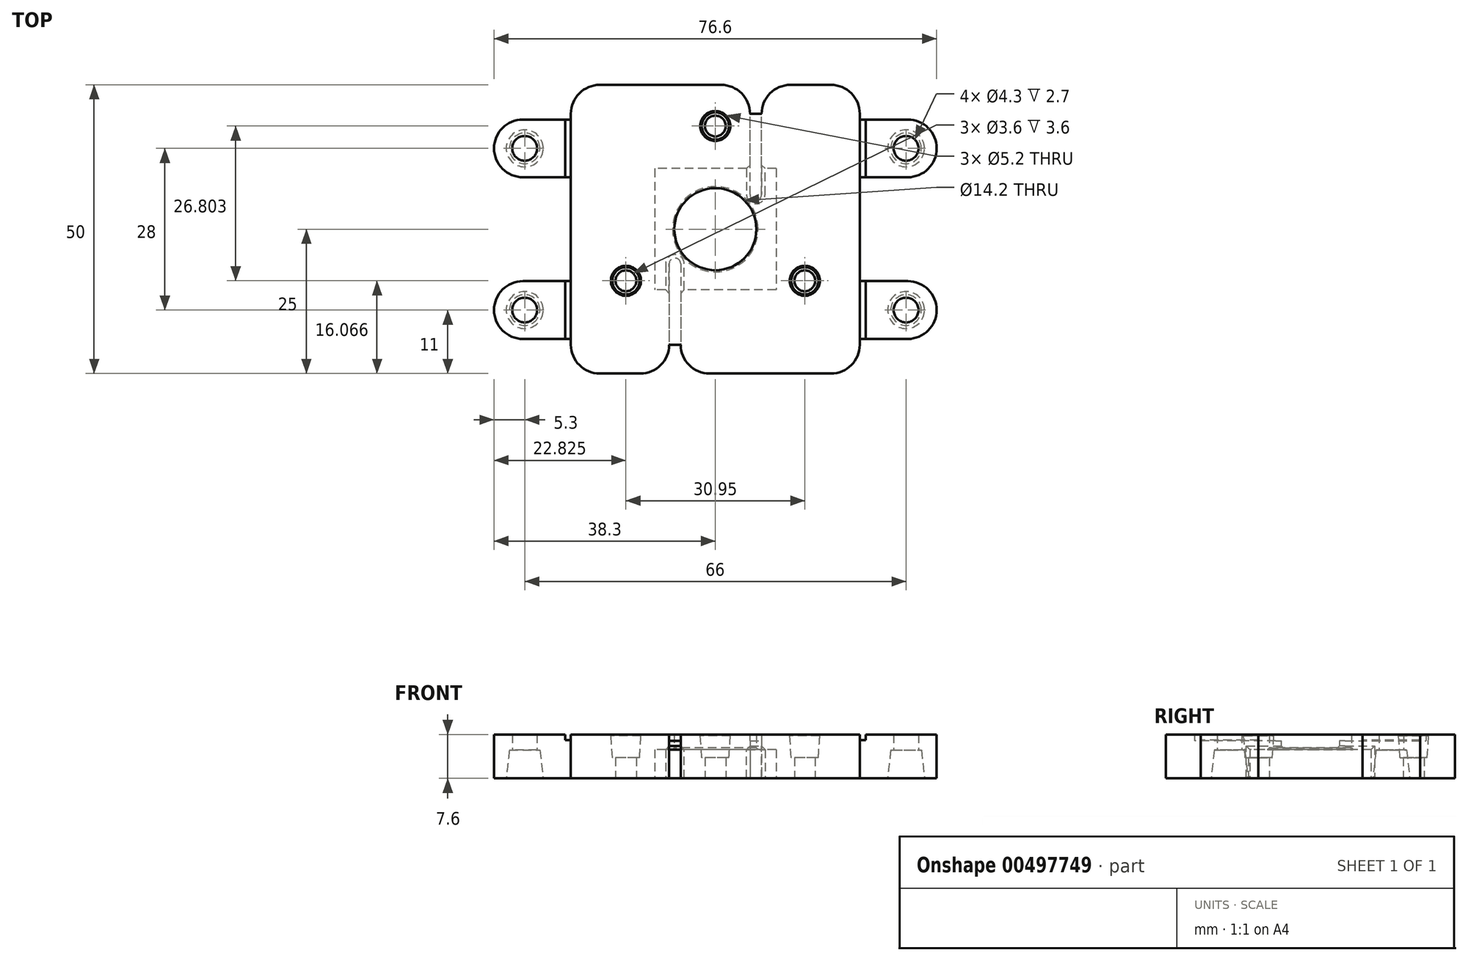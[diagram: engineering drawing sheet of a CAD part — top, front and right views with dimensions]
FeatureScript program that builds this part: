
annotation { "Feature Type Name" : "Feature", "Feature Type Description" : "" }
export const myFeature = defineFeature(function(context is Context, id is Id, definition is map)
    precondition{}
    {
        {
            var Q0;
            Q0=qCreatedBy(makeId("Top.planeOp"),FACE);
            var sketch = newSketch(context, id + "F0", { "sketchPlane" : qUnion([Q0])});
            skLineSegment(sketch, "E0.bottom", {"start": v(10.5, 10.5) * mm, "end": v(-10.5, 10.5) * mm});
            skLineSegment(sketch, "E0.top", {"start": v(10.5, -10.5) * mm, "end": v(-10.5, -10.5) * mm});
            skLineSegment(sketch, "E0.left", {"start": v(10.5, 10.5) * mm, "end": v(10.5, -10.5) * mm});
            skLineSegment(sketch, "E0.right", {"start": v(-10.5, 10.5) * mm, "end": v(-10.5, -10.5) * mm});
            skPoint(sketch, "E0.middle", {"position": v(0, 0) * mm});
            skLineSegment(sketch, "E1.bottom", {"start": v(25, 25) * mm, "end": v(-25, 25) * mm});
            skLineSegment(sketch, "E1.top", {"start": v(25, -25) * mm, "end": v(-25, -25) * mm});
            skLineSegment(sketch, "E1.left", {"start": v(25, 25) * mm, "end": v(25, -25) * mm});
            skLineSegment(sketch, "E1.right", {"start": v(-25, 25) * mm, "end": v(-25, -25) * mm});
            skCircle(sketch, "E2", {"center": v(-15.48, -8.93) * mm, "radius": 1.8 * mm});
            skCircle(sketch, "E3", {"center": v(0, 17.87) * mm, "radius": 1.8 * mm});
            skCircle(sketch, "E4", {"center": v(15.47, -8.93) * mm, "radius": 1.8 * mm});
            skLineSegment(sketch, "E5", {"start": v(-15.48, -8.93) * mm, "end": v(0, 17.87) * mm, "construction": true});
            skLineSegment(sketch, "E6", {"start": v(15.48, -8.93) * mm, "end": v(0, 17.87) * mm, "construction": true});
            skLineSegment(sketch, "E7", {"start": v(15.47, -8.93) * mm, "end": v(-15.48, -8.93) * mm, "construction": true});
            skCircle(sketch, "E8", {"center": v(0, 0) * mm, "radius": 17.87 * mm, "construction": true});
            skLineSegment(sketch, "E9.bottom", {"start": v(-25, 19) * mm, "end": v(-38.3, 19) * mm});
            skLineSegment(sketch, "E9.top", {"start": v(-25, 9) * mm, "end": v(-38.3, 9) * mm});
            skLineSegment(sketch, "E9.left", {"start": v(-25, 19) * mm, "end": v(-25, 9) * mm});
            skLineSegment(sketch, "E9.right", {"start": v(-38.3, 19) * mm, "end": v(-38.3, 9) * mm});
            skCircle(sketch, "E10", {"center": v(-33, 14) * mm, "radius": 2.15 * mm});
            skPoint(sketch, "E10.centerSnap0", {"position": v(-38.3, 14) * mm});
            skLineSegment(sketch, "E11.MirrorCS", {"start": v(38.3, 19) * mm, "end": v(38.3, 9) * mm});
            skLineSegment(sketch, "E12.MirrorCS", {"start": v(25, 19) * mm, "end": v(38.3, 19) * mm});
            skLineSegment(sketch, "E13.MirrorCS", {"start": v(25, 9) * mm, "end": v(38.3, 9) * mm});
            skCircle(sketch, "E14.MirrorC", {"center": v(33, 14) * mm, "radius": 2.15 * mm});
            skLineSegment(sketch, "E15.MirrorCS", {"start": v(-25, -9) * mm, "end": v(-38.3, -9) * mm});
            skLineSegment(sketch, "E16.MirrorCS", {"start": v(-25, -19) * mm, "end": v(-38.3, -19) * mm});
            skCircle(sketch, "E17.MirrorC", {"center": v(-33, -14) * mm, "radius": 2.15 * mm});
            skLineSegment(sketch, "E18.MirrorCS", {"start": v(25, -9) * mm, "end": v(38.3, -9) * mm});
            skLineSegment(sketch, "E19.MirrorCS", {"start": v(38.3, -19) * mm, "end": v(38.3, -9) * mm});
            skLineSegment(sketch, "E20.MirrorCS", {"start": v(25, -19) * mm, "end": v(38.3, -19) * mm});
            skCircle(sketch, "E21.MirrorC", {"center": v(33, -14) * mm, "radius": 2.15 * mm});
            skLineSegment(sketch, "E22.MirrorCS", {"start": v(-38.3, -19) * mm, "end": v(-38.3, -9) * mm});
            skLineSegment(sketch, "E23", {"start": v(6, 10.5) * mm, "end": v(6, 5) * mm});
            skLineSegment(sketch, "E24", {"start": v(6, 5) * mm, "end": v(8, 5) * mm});
            skLineSegment(sketch, "E25", {"start": v(8, 5) * mm, "end": v(8, 10.5) * mm});
            skLineSegment(sketch, "E26", {"start": v(-8, -10.5) * mm, "end": v(-8, -5) * mm});
            skLineSegment(sketch, "E27", {"start": v(-8, -5) * mm, "end": v(-6, -5) * mm});
            skLineSegment(sketch, "E28", {"start": v(-6, -5) * mm, "end": v(-6, -10.5) * mm});
            skLineSegment(sketch, "E29", {"start": v(6, 10.5) * mm, "end": v(6, 25) * mm});
            skLineSegment(sketch, "E30", {"start": v(8, 10.5) * mm, "end": v(8, 25) * mm});
            skLineSegment(sketch, "E31", {"start": v(-8, -10.5) * mm, "end": v(-8, -25) * mm});
            skLineSegment(sketch, "E32", {"start": v(-6, -10.5) * mm, "end": v(-6, -25) * mm});
            skCircle(sketch, "E33", {"center": v(0, 0) * mm, "radius": 7.1 * mm});
            skSolve(sketch);
        }
        {
            var Q0;
            {var subQ9=sQuery(id+"F0.wireOp",EDGE,"E0.right");Q0=makeQuery(id+"F0.imprint","IMPRINT",FACE,{"disambiguationData":[TD([[makeQuery(id+"F0.imprint","IMPRINT",EDGE,{"derivedFrom":subQ9}),-1.0]])]});}
            var Q1;
            {var subQ8=sQuery(id+"F0.wireOp",EDGE,"E0.left");Q1=makeQuery(id+"F0.imprint","IMPRINT",FACE,{"disambiguationData":[TD([[makeQuery(id+"F0.imprint","IMPRINT",EDGE,{"derivedFrom":subQ8}),1.0]])]});}
            var Q2;
            Q2=makeQuery(id+"F0.imprint","IMPRINT",FACE,{"disambiguationData":[TD([[makeQuery(id+"F0.imprint","IMPRINT",EDGE,{"derivedFrom":sQuery(id+"F0.wireOp",EDGE,"E9.bottom")}),1.0]])]});
            var Q3;
            {var subQ0=sQuery(id+"F0.wireOp",EDGE,"E15.MirrorCS");Q3=makeQuery(id+"F0.imprint","IMPRINT",FACE,{"disambiguationData":[TD([[makeQuery(id+"F0.imprint","IMPRINT",EDGE,{"derivedFrom":subQ0}),1.0]])]});}
            var Q4;
            {var subQ1=sQuery(id+"F0.wireOp",EDGE,"E18.MirrorCS");Q4=makeQuery(id+"F0.imprint","IMPRINT",FACE,{"disambiguationData":[TD([[makeQuery(id+"F0.imprint","IMPRINT",EDGE,{"derivedFrom":subQ1}),-1.0]])]});}
            var Q5;
            Q5=makeQuery(id+"F0.imprint","IMPRINT",FACE,{"disambiguationData":[TD([[makeQuery(id+"F0.imprint","IMPRINT",EDGE,{"derivedFrom":sQuery(id+"F0.wireOp",EDGE,"E11.MirrorCS")}),-1.0]])]});
            extrude(context, id + "F1", {"entities" : qUnion([Q0, Q1, Q2, Q3, Q4, Q5]), "depth" : (7.9 - 1.9) * mm, "offsetDistance" : 25 * mm});
        }
        {
            var Q0;
            Q0=makeQuery(id+"F1.opExtrude","CAP_FACE",FACE,{"disambiguationData":[OSD([sQuery(id+"F0.wireOp",EDGE,"E0.bottom"),sQuery(id+"F0.wireOp",EDGE,"E0.top"),sQuery(id+"F0.wireOp",EDGE,"E0.right"),sQuery(id+"F0.wireOp",EDGE,"E1.bottom"),sQuery(id+"F0.wireOp",EDGE,"E1.top"),sQuery(id+"F0.wireOp",EDGE,"E1.right"),sQuery(id+"F0.wireOp",EDGE,"E2"),sQuery(id+"F0.wireOp",EDGE,"E3"),sQuery(id+"F0.wireOp",EDGE,"E9.bottom"),sQuery(id+"F0.wireOp",EDGE,"E9.top"),sQuery(id+"F0.wireOp",EDGE,"E9.right"),sQuery(id+"F0.wireOp",EDGE,"E10"),sQuery(id+"F0.wireOp",EDGE,"E15.MirrorCS"),sQuery(id+"F0.wireOp",EDGE,"E16.MirrorCS"),sQuery(id+"F0.wireOp",EDGE,"E17.MirrorC"),sQuery(id+"F0.wireOp",EDGE,"E22.MirrorCS"),sQuery(id+"F0.wireOp",EDGE,"E29"),sQuery(id+"F0.wireOp",EDGE,"E31")])],"isStart":false});
            var sketch = newSketch(context, id + "F2", { "sketchPlane" : qUnion([Q0])});
            skCircle(sketch, "E34.0", {"center": v(0, 0) * mm, "radius": 7.1 * mm});
            skLineSegment(sketch, "E35.0", {"start": v(25, 25) * mm, "end": v(-25, 25) * mm});
            skLineSegment(sketch, "E35.1", {"start": v(-25, 25) * mm, "end": v(-25, -25) * mm});
            skLineSegment(sketch, "E35.2", {"start": v(25, 25) * mm, "end": v(25, -25) * mm});
            skLineSegment(sketch, "E35.3", {"start": v(25, -25) * mm, "end": v(-25, -25) * mm});
            skLineSegment(sketch, "E36.0", {"start": v(-6, -10.5) * mm, "end": v(-6, -25) * mm});
            skLineSegment(sketch, "E36.1", {"start": v(-8, -10.5) * mm, "end": v(-8, -25) * mm});
            skLineSegment(sketch, "E36.2", {"start": v(-8, -10.5) * mm, "end": v(-8, -5) * mm});
            skLineSegment(sketch, "E36.3", {"start": v(-8, -5) * mm, "end": v(-6, -5) * mm});
            skLineSegment(sketch, "E36.4", {"start": v(-6, -5) * mm, "end": v(-6, -10.5) * mm});
            skLineSegment(sketch, "E36.5", {"start": v(6, 10.5) * mm, "end": v(6, 5) * mm});
            skLineSegment(sketch, "E36.6", {"start": v(6, 5) * mm, "end": v(8, 5) * mm});
            skLineSegment(sketch, "E36.7", {"start": v(8, 5) * mm, "end": v(8, 10.5) * mm});
            skLineSegment(sketch, "E36.8", {"start": v(6, 10.5) * mm, "end": v(6, 25) * mm});
            skLineSegment(sketch, "E36.9", {"start": v(8, 10.5) * mm, "end": v(8, 25) * mm});
            skLineSegment(sketch, "E37.0", {"start": v(25, -9) * mm, "end": v(38.3, -9) * mm});
            skLineSegment(sketch, "E37.1", {"start": v(38.3, -19) * mm, "end": v(38.3, -9) * mm});
            skLineSegment(sketch, "E37.2", {"start": v(38.3, 19) * mm, "end": v(38.3, 9) * mm});
            skLineSegment(sketch, "E37.3", {"start": v(25, 19) * mm, "end": v(38.3, 19) * mm});
            skLineSegment(sketch, "E37.4", {"start": v(25, 9) * mm, "end": v(38.3, 9) * mm});
            skLineSegment(sketch, "E37.5", {"start": v(25, -19) * mm, "end": v(38.3, -19) * mm});
            skCircle(sketch, "E38.0", {"center": v(33, 14) * mm, "radius": 2.15 * mm});
            skCircle(sketch, "E38.1", {"center": v(33, -14) * mm, "radius": 2.15 * mm});
            skPoint(sketch, "E39.0", {"position": v(0, 17.87) * mm});
            skPoint(sketch, "E39.1", {"position": v(-15.48, -8.93) * mm});
            skPoint(sketch, "E39.2", {"position": v(15.48, -8.93) * mm});
            skCircle(sketch, "E40.0", {"center": v(15.47, -8.93) * mm, "radius": 1.8 * mm});
            skCircle(sketch, "E41.0", {"center": v(0, 17.87) * mm, "radius": 1.8 * mm});
            skCircle(sketch, "E41.1", {"center": v(-15.48, -8.93) * mm, "radius": 1.8 * mm});
            skSolve(sketch);
        }
        {
            var Q0;
            {var subQ6=sQuery(id+"F2.wireOp",EDGE,"E36.1");Q0=makeQuery(id+"F2.imprint","IMPRINT",FACE,{"disambiguationData":[TD([[makeQuery(id+"F2.imprint","IMPRINT",EDGE,{"derivedFrom":subQ6}),-1.0]])]});}
            var Q1;
            Q1=makeQuery(id+"F2.imprint","IMPRINT",FACE,{"disambiguationData":[TD([[makeQuery(id+"F2.imprint","IMPRINT",EDGE,{"derivedFrom":sQuery(id+"F2.wireOp",EDGE,"E34.0")}),-1.0]])]});
            var Q2;
            {var subQ1=makeQuery(id+"F1.opExtrude","CAP_EDGE",EDGE,{"disambiguationData":[OSD([sQuery(id+"F0.wireOp",EDGE,"E15.MirrorCS")])],"isStart":false});Q2=makeQuery(id+"F2.imprint","IMPRINT",FACE,{"disambiguationData":[TD([[makeQuery(id+"F2.imprint","IMPRINT",EDGE,{"derivedFrom":subQ1}),1.0]])]});}
            var Q3;
            {var subQ0=makeQuery(id+"F1.opExtrude","CAP_EDGE",EDGE,{"disambiguationData":[OSD([sQuery(id+"F0.wireOp",EDGE,"E9.bottom")])],"isStart":false});Q3=makeQuery(id+"F2.imprint","IMPRINT",FACE,{"disambiguationData":[TD([[makeQuery(id+"F2.imprint","IMPRINT",EDGE,{"derivedFrom":subQ0}),1.0]])]});}
            var Q4;
            Q4=makeQuery(id+"F2.imprint","IMPRINT",FACE,{"disambiguationData":[TD([[makeQuery(id+"F2.imprint","IMPRINT",EDGE,{"derivedFrom":sQuery(id+"F2.wireOp",EDGE,"E37.2")}),-1.0]])]});
            var Q5;
            {var subQ0=sQuery(id+"F2.wireOp",EDGE,"E37.0");Q5=makeQuery(id+"F2.imprint","IMPRINT",FACE,{"disambiguationData":[TD([[makeQuery(id+"F2.imprint","IMPRINT",EDGE,{"derivedFrom":subQ0}),-1.0]])]});}
            var Q6;
            Q6=makeQuery(id+"F2.imprint","IMPRINT",FACE,{"disambiguationData":[TD([[makeQuery(id+"F2.imprint","IMPRINT",EDGE,{"derivedFrom":sQuery(id+"F2.wireOp",EDGE,"hlMW5f2f-XIVy-xnIR-Iq4x-g7ZeSHMqcFU1")}),1.0]])]});
            var Q7;
            Q7=makeQuery(id+"F2.imprint","IMPRINT",FACE,{"disambiguationData":[TD([[makeQuery(id+"F2.imprint","IMPRINT",EDGE,{"derivedFrom":sQuery(id+"F2.wireOp",EDGE,"uH5zLlzq-hMVk-IZsu-RLze-oHsLc7MtS3rd")}),1.0]])]});
            var Q8;
            Q8=makeQuery(id+"F2.imprint","IMPRINT",FACE,{"disambiguationData":[TD([[makeQuery(id+"F2.imprint","IMPRINT",EDGE,{"derivedFrom":sQuery(id+"F2.wireOp",EDGE,"2zK1Z5qS-e3uA-KtzF-qnvm-I0SGlEl2r4kh")}),1.0]])]});
            extrude(context, id + "F3", {"entities" : qUnion([Q0, Q1, Q2, Q3, Q4, Q5, Q6, Q7, Q8]), "operationType" : NewBodyOperationType.ADD, "depth" : (4.5 - 1.9) * mm, "offsetDistance" : 25 * mm});
        }
        {
            var Q0;
            Q0=makeQuery(id+"F13.boolean.opBoolean","MERGE",FACE,{"derivedFrom":[makeQuery(id+"F3.opExtrude","CAP_FACE",FACE,{"disambiguationData":[OSD([sQuery(id+"F0.wireOp",EDGE,"E9.bottom"),sQuery(id+"F0.wireOp",EDGE,"E9.top"),sQuery(id+"F0.wireOp",EDGE,"E9.right"),sQuery(id+"F0.wireOp",EDGE,"E10"),sQuery(id+"F0.wireOp",EDGE,"E15.MirrorCS"),sQuery(id+"F0.wireOp",EDGE,"E16.MirrorCS"),sQuery(id+"F0.wireOp",EDGE,"E17.MirrorC"),sQuery(id+"F0.wireOp",EDGE,"E22.MirrorCS"),sQuery(id+"F2.wireOp",EDGE,"E34.0"),sQuery(id+"F2.wireOp",EDGE,"E35.0"),sQuery(id+"F2.wireOp",EDGE,"E35.1"),sQuery(id+"F2.wireOp",EDGE,"E35.2"),sQuery(id+"F2.wireOp",EDGE,"E35.3"),sQuery(id+"F2.wireOp",EDGE,"E36.0"),sQuery(id+"F2.wireOp",EDGE,"E36.1"),sQuery(id+"F2.wireOp",EDGE,"E36.2"),sQuery(id+"F2.wireOp",EDGE,"E36.3"),sQuery(id+"F2.wireOp",EDGE,"E36.4"),sQuery(id+"F2.wireOp",EDGE,"E36.5"),sQuery(id+"F2.wireOp",EDGE,"E36.6"),sQuery(id+"F2.wireOp",EDGE,"E36.7"),sQuery(id+"F2.wireOp",EDGE,"E36.8"),sQuery(id+"F2.wireOp",EDGE,"E36.9"),sQuery(id+"F2.wireOp",EDGE,"E37.0"),sQuery(id+"F2.wireOp",EDGE,"E37.1"),sQuery(id+"F2.wireOp",EDGE,"E37.2"),sQuery(id+"F2.wireOp",EDGE,"E37.3"),sQuery(id+"F2.wireOp",EDGE,"E37.4"),sQuery(id+"F2.wireOp",EDGE,"E37.5"),sQuery(id+"F2.wireOp",EDGE,"E38.0"),sQuery(id+"F2.wireOp",EDGE,"E38.1"),sQuery(id+"F2.wireOp",EDGE,"E40.0"),sQuery(id+"F2.wireOp",EDGE,"E41.0"),sQuery(id+"F2.wireOp",EDGE,"E41.1")])],"isStart":false}),makeQuery(id+"F13.opExtrude","CAP_FACE",FACE,{"disambiguationData":[OSD([sQuery(id+"F12.wireOp",EDGE,"E50.0"),sQuery(id+"F12.wireOp",EDGE,"E50.1"),sQuery(id+"F12.wireOp",EDGE,"E50.2"),sQuery(id+"F12.wireOp",EDGE,"E52")])],"isStart":true}),makeQuery(id+"F13.opExtrude","CAP_FACE",FACE,{"disambiguationData":[OSD([sQuery(id+"F12.wireOp",EDGE,"E50.4"),sQuery(id+"F12.wireOp",EDGE,"E50.5"),sQuery(id+"F12.wireOp",EDGE,"E50.6"),sQuery(id+"F12.wireOp",EDGE,"E51")])],"isStart":true})]});
            var sketch = newSketch(context, id + "F4", { "sketchPlane" : qUnion([Q0])});
            skCircle(sketch, "E42.0", {"center": v(-15.48, -8.93) * mm, "radius": 1.8 * mm, "construction": true});
            skCircle(sketch, "E42.1", {"center": v(15.47, -8.93) * mm, "radius": 1.8 * mm, "construction": true});
            skCircle(sketch, "E42.2", {"center": v(0, 17.87) * mm, "radius": 1.8 * mm, "construction": true});
            skCircle(sketch, "E43", {"center": v(-15.48, -8.93) * mm, "radius": 2.6 * mm});
            skCircle(sketch, "E44", {"center": v(15.47, -8.93) * mm, "radius": 2.6 * mm});
            skCircle(sketch, "E45", {"center": v(0, 17.87) * mm, "radius": 2.6 * mm});
            skLineSegment(sketch, "E46", {"start": v(-25, 19) * mm, "end": v(-25, -19) * mm});
            skLineSegment(sketch, "E47", {"start": v(25, 19) * mm, "end": v(25, -19) * mm});
            skLineSegment(sketch, "E48", {"start": v(-26, 19) * mm, "end": v(-26, -19) * mm});
            skLineSegment(sketch, "E49", {"start": v(26, 19) * mm, "end": v(26, -19) * mm});
            skSolve(sketch);
        }
        {
            var Q0;
            Q0=makeQuery(id+"F4.imprint","IMPRINT",FACE,{"disambiguationData":[TD([[makeQuery(id+"F4.imprint","IMPRINT",EDGE,{"derivedFrom":sQuery(id+"F4.wireOp",EDGE,"E43")}),1.0]])]});
            var Q1;
            Q1=makeQuery(id+"F4.imprint","IMPRINT",FACE,{"disambiguationData":[TD([[makeQuery(id+"F4.imprint","IMPRINT",EDGE,{"derivedFrom":sQuery(id+"F4.wireOp",EDGE,"E45")}),1.0]])]});
            var Q2;
            Q2=makeQuery(id+"F4.imprint","IMPRINT",FACE,{"disambiguationData":[TD([[makeQuery(id+"F4.imprint","IMPRINT",EDGE,{"derivedFrom":sQuery(id+"F4.wireOp",EDGE,"E44")}),1.0]])]});
            extrude(context, id + "F5", {"entities" : qUnion([Q0, Q1, Q2]), "operationType" : NewBodyOperationType.REMOVE, "oppositeDirection" : true, "depth" : 4 * mm, "offsetDistance" : 25 * mm});
        }
        {
            var Q0;
            {var subQ1=sQuery(id+"F0.wireOp",EDGE,"E9.bottom");var subQ2=makeQuery(id+"F3.opExtrude","CAP_EDGE",EDGE,{"disambiguationData":[OSD([subQ1])],"isStart":false});var subQ7=sQuery(id+"F4.wireOp",EDGE,"E48");var subQ8=makeQuery(id+"F4.imprint","INTERSECT",VERTEX,{"derivedFrom":[subQ2,subQ7]});Q0=makeQuery(id+"F4.imprint","IMPRINT",FACE,{"disambiguationData":[TD([[makeQuery(id+"F4.imprint","IMPRINT",EDGE,{"disambiguationData":[TD([[subQ8,-1.0]])],"derivedFrom":subQ7}),1.0]])]});}
            var Q1;
            {var subQ3=sQuery(id+"F0.wireOp",EDGE,"E16.MirrorCS");var subQ4=makeQuery(id+"F3.opExtrude","CAP_EDGE",EDGE,{"disambiguationData":[OSD([subQ3])],"isStart":false});var subQ7=sQuery(id+"F4.wireOp",EDGE,"E48");var subQ8=makeQuery(id+"F4.imprint","INTERSECT",VERTEX,{"derivedFrom":[subQ4,subQ7]});Q1=makeQuery(id+"F4.imprint","IMPRINT",FACE,{"disambiguationData":[TD([[makeQuery(id+"F4.imprint","IMPRINT",EDGE,{"disambiguationData":[TD([[subQ8,1.0]])],"derivedFrom":subQ7}),1.0]])]});}
            var Q2;
            {var subQ3=sQuery(id+"F2.wireOp",EDGE,"E37.5");var subQ4=makeQuery(id+"F3.opExtrude","CAP_EDGE",EDGE,{"disambiguationData":[OSD([subQ3])],"isStart":false});var subQ7=sQuery(id+"F4.wireOp",EDGE,"E49");var subQ8=makeQuery(id+"F4.imprint","INTERSECT",VERTEX,{"derivedFrom":[subQ4,subQ7]});Q2=makeQuery(id+"F4.imprint","IMPRINT",FACE,{"disambiguationData":[TD([[makeQuery(id+"F4.imprint","IMPRINT",EDGE,{"disambiguationData":[TD([[subQ8,1.0]])],"derivedFrom":subQ7}),-1.0]])]});}
            var Q3;
            {var subQ1=sQuery(id+"F2.wireOp",EDGE,"E37.3");var subQ2=makeQuery(id+"F3.opExtrude","CAP_EDGE",EDGE,{"disambiguationData":[OSD([subQ1])],"isStart":false});var subQ7=sQuery(id+"F4.wireOp",EDGE,"E49");var subQ9=makeQuery(id+"F4.imprint","INTERSECT",VERTEX,{"derivedFrom":[subQ2,subQ7]});Q3=makeQuery(id+"F4.imprint","IMPRINT",FACE,{"disambiguationData":[TD([[makeQuery(id+"F4.imprint","IMPRINT",EDGE,{"disambiguationData":[TD([[subQ9,-1.0]])],"derivedFrom":subQ7}),-1.0]])]});}
            extrude(context, id + "F6", {"entities" : qUnion([Q0, Q1, Q2, Q3]), "operationType" : NewBodyOperationType.REMOVE, "oppositeDirection" : true, "depth" : 1 * mm, "offsetDistance" : 25 * mm});
        }
        {
            var Q0;
            Q0=makeQuery(id+"F3.opExtrude","SWEPT_EDGE",EDGE,{"disambiguationData":[OSD([sQuery(id+"F2.wireOp",EDGE,"E36.3"),sQuery(id+"F2.wireOp",EDGE,"E36.4")])]});
            var Q1;
            Q1=makeQuery(id+"F3.opExtrude","SWEPT_EDGE",EDGE,{"disambiguationData":[OSD([sQuery(id+"F2.wireOp",EDGE,"E36.2"),sQuery(id+"F2.wireOp",EDGE,"E36.3")])]});
            var Q2;
            Q2=makeQuery(id+"F3.opExtrude","SWEPT_EDGE",EDGE,{"disambiguationData":[OSD([sQuery(id+"F2.wireOp",EDGE,"E36.5"),sQuery(id+"F2.wireOp",EDGE,"E36.6")])]});
            var Q3;
            Q3=makeQuery(id+"F3.opExtrude","SWEPT_EDGE",EDGE,{"disambiguationData":[OSD([sQuery(id+"F2.wireOp",EDGE,"E36.6"),sQuery(id+"F2.wireOp",EDGE,"E36.7")])]});
            fillet(context, id + "F7", {"entities" : qUnion([Q0, Q1, Q2, Q3]), "radius" : 1 * mm, "tangentPropagation" : true, "allowEdgeOverflow" : false});
        }
        {
            var Q0;
            Q0=makeQuery(id+"F1.opExtrude","SWEPT_EDGE",EDGE,{"disambiguationData":[OSD([sQuery(id+"F0.wireOp",EDGE,"E9.top"),sQuery(id+"F0.wireOp",EDGE,"E9.right")])]});
            var Q1;
            Q1=makeQuery(id+"F1.opExtrude","SWEPT_EDGE",EDGE,{"disambiguationData":[OSD([sQuery(id+"F0.wireOp",EDGE,"E9.bottom"),sQuery(id+"F0.wireOp",EDGE,"E9.right")])]});
            var Q2;
            Q2=makeQuery(id+"F1.opExtrude","SWEPT_EDGE",EDGE,{"disambiguationData":[OSD([sQuery(id+"F0.wireOp",EDGE,"E16.MirrorCS"),sQuery(id+"F0.wireOp",EDGE,"E22.MirrorCS")])]});
            var Q3;
            Q3=makeQuery(id+"F1.opExtrude","SWEPT_EDGE",EDGE,{"disambiguationData":[OSD([sQuery(id+"F0.wireOp",EDGE,"E15.MirrorCS"),sQuery(id+"F0.wireOp",EDGE,"E22.MirrorCS")])]});
            var Q4;
            Q4=makeQuery(id+"F1.opExtrude","SWEPT_EDGE",EDGE,{"disambiguationData":[OSD([sQuery(id+"F0.wireOp",EDGE,"E19.MirrorCS"),sQuery(id+"F0.wireOp",EDGE,"E20.MirrorCS")])]});
            var Q5;
            Q5=makeQuery(id+"F1.opExtrude","SWEPT_EDGE",EDGE,{"disambiguationData":[OSD([sQuery(id+"F0.wireOp",EDGE,"E18.MirrorCS"),sQuery(id+"F0.wireOp",EDGE,"E19.MirrorCS")])]});
            var Q6;
            Q6=makeQuery(id+"F1.opExtrude","SWEPT_EDGE",EDGE,{"disambiguationData":[OSD([sQuery(id+"F0.wireOp",EDGE,"E11.MirrorCS"),sQuery(id+"F0.wireOp",EDGE,"E13.MirrorCS")])]});
            var Q7;
            Q7=makeQuery(id+"F1.opExtrude","SWEPT_EDGE",EDGE,{"disambiguationData":[OSD([sQuery(id+"F0.wireOp",EDGE,"E11.MirrorCS"),sQuery(id+"F0.wireOp",EDGE,"E12.MirrorCS")])]});
            var Q8;
            Q8=makeQuery(id+"F3.boolean.opBoolean","MERGE",EDGE,{"derivedFrom":[makeQuery(id+"F1.opExtrude","SWEPT_EDGE",EDGE,{"disambiguationData":[OSD([sQuery(id+"F0.wireOp",EDGE,"E1.top"),sQuery(id+"F0.wireOp",EDGE,"E1.right")])]}),makeQuery(id+"F3.opExtrude","SWEPT_EDGE",EDGE,{"disambiguationData":[OSD([sQuery(id+"F2.wireOp",EDGE,"E35.1"),sQuery(id+"F2.wireOp",EDGE,"E35.3")])]})]});
            var Q9;
            Q9=makeQuery(id+"F3.boolean.opBoolean","MERGE",EDGE,{"derivedFrom":[makeQuery(id+"F1.opExtrude","SWEPT_EDGE",EDGE,{"disambiguationData":[OSD([sQuery(id+"F0.wireOp",EDGE,"E1.top"),sQuery(id+"F0.wireOp",EDGE,"E1.left")])]}),makeQuery(id+"F3.opExtrude","SWEPT_EDGE",EDGE,{"disambiguationData":[OSD([sQuery(id+"F2.wireOp",EDGE,"E35.2"),sQuery(id+"F2.wireOp",EDGE,"E35.3")])]})]});
            var Q10;
            Q10=makeQuery(id+"F3.boolean.opBoolean","MERGE",EDGE,{"derivedFrom":[makeQuery(id+"F1.opExtrude","SWEPT_EDGE",EDGE,{"disambiguationData":[OSD([sQuery(id+"F0.wireOp",EDGE,"E1.bottom"),sQuery(id+"F0.wireOp",EDGE,"E1.left")])]}),makeQuery(id+"F3.opExtrude","SWEPT_EDGE",EDGE,{"disambiguationData":[OSD([sQuery(id+"F2.wireOp",EDGE,"E35.0"),sQuery(id+"F2.wireOp",EDGE,"E35.2")])]})]});
            var Q11;
            Q11=makeQuery(id+"F3.boolean.opBoolean","MERGE",EDGE,{"derivedFrom":[makeQuery(id+"F1.opExtrude","SWEPT_EDGE",EDGE,{"disambiguationData":[OSD([sQuery(id+"F0.wireOp",EDGE,"E1.bottom"),sQuery(id+"F0.wireOp",EDGE,"E1.right")])]}),makeQuery(id+"F3.opExtrude","SWEPT_EDGE",EDGE,{"disambiguationData":[OSD([sQuery(id+"F2.wireOp",EDGE,"E35.0"),sQuery(id+"F2.wireOp",EDGE,"E35.1")])]})]});
            var Q12;
            Q12=makeQuery(id+"F3.boolean.opBoolean","MERGE",EDGE,{"derivedFrom":[makeQuery(id+"F1.opExtrude","SWEPT_EDGE",EDGE,{"disambiguationData":[OSD([sQuery(id+"F0.wireOp",EDGE,"E1.bottom"),sQuery(id+"F0.wireOp",EDGE,"E29")])]}),makeQuery(id+"F3.opExtrude","SWEPT_EDGE",EDGE,{"disambiguationData":[OSD([sQuery(id+"F2.wireOp",EDGE,"E35.0"),sQuery(id+"F2.wireOp",EDGE,"E36.8")])]})]});
            var Q13;
            Q13=makeQuery(id+"F3.boolean.opBoolean","MERGE",EDGE,{"derivedFrom":[makeQuery(id+"F1.opExtrude","SWEPT_EDGE",EDGE,{"disambiguationData":[OSD([sQuery(id+"F0.wireOp",EDGE,"E1.bottom"),sQuery(id+"F0.wireOp",EDGE,"E30")])]}),makeQuery(id+"F3.opExtrude","SWEPT_EDGE",EDGE,{"disambiguationData":[OSD([sQuery(id+"F2.wireOp",EDGE,"E35.0"),sQuery(id+"F2.wireOp",EDGE,"E36.9")])]})]});
            var Q14;
            Q14=makeQuery(id+"F3.boolean.opBoolean","MERGE",EDGE,{"derivedFrom":[makeQuery(id+"F1.opExtrude","SWEPT_EDGE",EDGE,{"disambiguationData":[OSD([sQuery(id+"F0.wireOp",EDGE,"E1.top"),sQuery(id+"F0.wireOp",EDGE,"E31")])]}),makeQuery(id+"F3.opExtrude","SWEPT_EDGE",EDGE,{"disambiguationData":[OSD([sQuery(id+"F2.wireOp",EDGE,"E35.3"),sQuery(id+"F2.wireOp",EDGE,"E36.1")])]})]});
            var Q15;
            Q15=makeQuery(id+"F3.boolean.opBoolean","MERGE",EDGE,{"derivedFrom":[makeQuery(id+"F1.opExtrude","SWEPT_EDGE",EDGE,{"disambiguationData":[OSD([sQuery(id+"F0.wireOp",EDGE,"E1.top"),sQuery(id+"F0.wireOp",EDGE,"E32")])]}),makeQuery(id+"F3.opExtrude","SWEPT_EDGE",EDGE,{"disambiguationData":[OSD([sQuery(id+"F2.wireOp",EDGE,"E35.3"),sQuery(id+"F2.wireOp",EDGE,"E36.0")])]})]});
            fillet(context, id + "F8", {"entities" : qUnion([Q0, Q1, Q2, Q3, Q4, Q5, Q6, Q7, Q8, Q9, Q10, Q11, Q12, Q13, Q14, Q15]), "radius" : 5 * mm, "tangentPropagation" : true, "allowEdgeOverflow" : false});
        }
        {
            var Q0;
            Q0=makeQuery(id+"F1.opExtrude","CAP_EDGE",EDGE,{"disambiguationData":[OSD([sQuery(id+"F0.wireOp",EDGE,"E0.right")])],"isStart":true});
            var Q1;
            {var subQ0=sQuery(id+"F0.wireOp",EDGE,"E0.top");Q1=makeQuery(id+"F1.opExtrude","CAP_EDGE",EDGE,{"disambiguationData":[OSD([subQ0]),TDD([makeQuery(id+"F0.imprint","IMPRINT",EDGE,{"disambiguationData":[TD([[makeQuery(id+"F0.imprint","INTERSECT",VERTEX,{"derivedFrom":[subQ0,sQuery(id+"F0.wireOp",EDGE,"E0.right")]}),1.0]])],"derivedFrom":subQ0})])],"isStart":true});}
            var Q2;
            {var subQ0=sQuery(id+"F0.wireOp",EDGE,"E0.top");Q2=makeQuery(id+"F1.opExtrude","CAP_EDGE",EDGE,{"disambiguationData":[OSD([subQ0]),TDD([makeQuery(id+"F0.imprint","IMPRINT",EDGE,{"disambiguationData":[TD([[makeQuery(id+"F0.imprint","INTERSECT",VERTEX,{"derivedFrom":[subQ0,sQuery(id+"F0.wireOp",EDGE,"E0.left")]}),-1.0]])],"derivedFrom":subQ0})])],"isStart":true});}
            var Q3;
            Q3=makeQuery(id+"F1.opExtrude","CAP_EDGE",EDGE,{"disambiguationData":[OSD([sQuery(id+"F0.wireOp",EDGE,"E0.left")])],"isStart":true});
            var Q4;
            {var subQ0=sQuery(id+"F0.wireOp",EDGE,"E0.bottom");Q4=makeQuery(id+"F1.opExtrude","CAP_EDGE",EDGE,{"disambiguationData":[OSD([subQ0]),TDD([makeQuery(id+"F0.imprint","IMPRINT",EDGE,{"disambiguationData":[TD([[makeQuery(id+"F0.imprint","INTERSECT",VERTEX,{"derivedFrom":[subQ0,sQuery(id+"F0.wireOp",EDGE,"E0.left")]}),-1.0]])],"derivedFrom":subQ0})])],"isStart":true});}
            var Q5;
            {var subQ0=sQuery(id+"F0.wireOp",EDGE,"E0.bottom");Q5=makeQuery(id+"F1.opExtrude","CAP_EDGE",EDGE,{"disambiguationData":[OSD([subQ0]),TDD([makeQuery(id+"F0.imprint","IMPRINT",EDGE,{"disambiguationData":[TD([[makeQuery(id+"F0.imprint","INTERSECT",VERTEX,{"derivedFrom":[subQ0,sQuery(id+"F0.wireOp",EDGE,"E0.right")]}),1.0]])],"derivedFrom":subQ0})])],"isStart":true});}
            var Q6;
            Q6=makeQuery(id+"F3.opExtrude","CAP_EDGE",EDGE,{"disambiguationData":[OSD([sQuery(id+"F2.wireOp",EDGE,"E36.0"),sQuery(id+"F2.wireOp",EDGE,"E36.4")])],"isStart":true});
            var Q7;
            Q7=makeQuery(id+"F3.opExtrude","CAP_EDGE",EDGE,{"disambiguationData":[OSD([sQuery(id+"F2.wireOp",EDGE,"E36.7"),sQuery(id+"F2.wireOp",EDGE,"E36.9")])],"isStart":true});
            var Q8;
            Q8=makeQuery(id+"F1.opExtrude","SWEPT_EDGE",EDGE,{"disambiguationData":[OSD([sQuery(id+"F0.wireOp",EDGE,"E0.top"),sQuery(id+"F0.wireOp",EDGE,"E26"),sQuery(id+"F0.wireOp",EDGE,"E31")])]});
            var Q9;
            Q9=makeQuery(id+"F1.opExtrude","SWEPT_EDGE",EDGE,{"disambiguationData":[OSD([sQuery(id+"F0.wireOp",EDGE,"E0.top"),sQuery(id+"F0.wireOp",EDGE,"E28"),sQuery(id+"F0.wireOp",EDGE,"E32")])]});
            var Q10;
            Q10=makeQuery(id+"F1.opExtrude","SWEPT_EDGE",EDGE,{"disambiguationData":[OSD([sQuery(id+"F0.wireOp",EDGE,"E0.bottom"),sQuery(id+"F0.wireOp",EDGE,"E23"),sQuery(id+"F0.wireOp",EDGE,"E29")])]});
            var Q11;
            Q11=makeQuery(id+"F1.opExtrude","SWEPT_EDGE",EDGE,{"disambiguationData":[OSD([sQuery(id+"F0.wireOp",EDGE,"E0.bottom"),sQuery(id+"F0.wireOp",EDGE,"E25"),sQuery(id+"F0.wireOp",EDGE,"E30")])]});
            chamfer(context, id + "F9", {"entities" : qUnion([Q0, Q1, Q2, Q3, Q4, Q5, Q6, Q7, Q8, Q9, Q10, Q11]), "width" : 0.6 * mm, "tangentPropagation" : true});
        }
        {
            var Q0;
            Q0=makeQuery(id+"F5.boolean.opBoolean","COPY",EDGE,{"derivedFrom":makeQuery(id+"F5.opExtrude","CAP_EDGE",EDGE,{"disambiguationData":[OSD([sQuery(id+"F4.wireOp",EDGE,"E44")])],"isStart":false})});
            var Q1;
            Q1=makeQuery(id+"F5.boolean.opBoolean","COPY",EDGE,{"derivedFrom":makeQuery(id+"F5.opExtrude","CAP_EDGE",EDGE,{"disambiguationData":[OSD([sQuery(id+"F4.wireOp",EDGE,"E43")])],"isStart":false})});
            var Q2;
            Q2=makeQuery(id+"F5.boolean.opBoolean","COPY",EDGE,{"derivedFrom":makeQuery(id+"F5.opExtrude","CAP_EDGE",EDGE,{"disambiguationData":[OSD([sQuery(id+"F4.wireOp",EDGE,"E45")])],"isStart":false})});
            chamfer(context, id + "F10", {"entities" : qUnion([Q0, Q1, Q2]), "chamferType" : ChamferType.TWO_OFFSETS, "width1" : 0.25 * mm, "oppositeDirection" : false, "width2" : 3.8 * mm, "tangentPropagation" : true});
        }
        {
            var Q0;
            {var subQ9=sQuery(id+"F0.wireOp",EDGE,"E0.right");Q0=makeQuery(id+"F0.imprint","IMPRINT",FACE,{"disambiguationData":[TD([[makeQuery(id+"F0.imprint","IMPRINT",EDGE,{"derivedFrom":subQ9}),-1.0]])]});}
            var Q1;
            {var subQ8=sQuery(id+"F0.wireOp",EDGE,"E0.left");Q1=makeQuery(id+"F0.imprint","IMPRINT",FACE,{"disambiguationData":[TD([[makeQuery(id+"F0.imprint","IMPRINT",EDGE,{"derivedFrom":subQ8}),1.0]])]});}
            var Q2;
            {var subQ0=sQuery(id+"F0.wireOp",EDGE,"E15.MirrorCS");Q2=makeQuery(id+"F0.imprint","IMPRINT",FACE,{"disambiguationData":[TD([[makeQuery(id+"F0.imprint","IMPRINT",EDGE,{"derivedFrom":subQ0}),1.0]])]});}
            var Q3;
            Q3=makeQuery(id+"F0.imprint","IMPRINT",FACE,{"disambiguationData":[TD([[makeQuery(id+"F0.imprint","IMPRINT",EDGE,{"derivedFrom":sQuery(id+"F0.wireOp",EDGE,"E9.bottom")}),1.0]])]});
            var Q4;
            Q4=makeQuery(id+"F0.imprint","IMPRINT",FACE,{"disambiguationData":[TD([[makeQuery(id+"F0.imprint","IMPRINT",EDGE,{"derivedFrom":sQuery(id+"F0.wireOp",EDGE,"E11.MirrorCS")}),-1.0]])]});
            var Q5;
            {var subQ1=sQuery(id+"F0.wireOp",EDGE,"E18.MirrorCS");Q5=makeQuery(id+"F0.imprint","IMPRINT",FACE,{"disambiguationData":[TD([[makeQuery(id+"F0.imprint","IMPRINT",EDGE,{"derivedFrom":subQ1}),-1.0]])]});}
            extrude(context, id + "F11", {"entities" : qUnion([Q0, Q1, Q2, Q3, Q4, Q5]), "operationType" : NewBodyOperationType.REMOVE, "depth" : 1 * mm, "offsetDistance" : 25 * mm});
        }
        {
            var Q0;
            Q0=makeQuery(id+"F3.opExtrude","CAP_FACE",FACE,{"disambiguationData":[OSD([sQuery(id+"F0.wireOp",EDGE,"E9.bottom"),sQuery(id+"F0.wireOp",EDGE,"E9.top"),sQuery(id+"F0.wireOp",EDGE,"E9.right"),sQuery(id+"F0.wireOp",EDGE,"E10"),sQuery(id+"F0.wireOp",EDGE,"E15.MirrorCS"),sQuery(id+"F0.wireOp",EDGE,"E16.MirrorCS"),sQuery(id+"F0.wireOp",EDGE,"E17.MirrorC"),sQuery(id+"F0.wireOp",EDGE,"E22.MirrorCS"),sQuery(id+"F2.wireOp",EDGE,"E34.0"),sQuery(id+"F2.wireOp",EDGE,"E35.0"),sQuery(id+"F2.wireOp",EDGE,"E35.1"),sQuery(id+"F2.wireOp",EDGE,"E35.2"),sQuery(id+"F2.wireOp",EDGE,"E35.3"),sQuery(id+"F2.wireOp",EDGE,"E36.0"),sQuery(id+"F2.wireOp",EDGE,"E36.1"),sQuery(id+"F2.wireOp",EDGE,"E36.2"),sQuery(id+"F2.wireOp",EDGE,"E36.3"),sQuery(id+"F2.wireOp",EDGE,"E36.4"),sQuery(id+"F2.wireOp",EDGE,"E36.5"),sQuery(id+"F2.wireOp",EDGE,"E36.6"),sQuery(id+"F2.wireOp",EDGE,"E36.7"),sQuery(id+"F2.wireOp",EDGE,"E36.8"),sQuery(id+"F2.wireOp",EDGE,"E36.9"),sQuery(id+"F2.wireOp",EDGE,"E37.0"),sQuery(id+"F2.wireOp",EDGE,"E37.1"),sQuery(id+"F2.wireOp",EDGE,"E37.2"),sQuery(id+"F2.wireOp",EDGE,"E37.3"),sQuery(id+"F2.wireOp",EDGE,"E37.4"),sQuery(id+"F2.wireOp",EDGE,"E37.5"),sQuery(id+"F2.wireOp",EDGE,"E38.0"),sQuery(id+"F2.wireOp",EDGE,"E38.1"),sQuery(id+"F2.wireOp",EDGE,"2zK1Z5qS-e3uA-KtzF-qnvm-I0SGlEl2r4kh"),sQuery(id+"F2.wireOp",EDGE,"hlMW5f2f-XIVy-xnIR-Iq4x-g7ZeSHMqcFU1"),sQuery(id+"F2.wireOp",EDGE,"uH5zLlzq-hMVk-IZsu-RLze-oHsLc7MtS3rd")])],"isStart":false});
            var sketch = newSketch(context, id + "F12", { "sketchPlane" : qUnion([Q0])});
            skLineSegment(sketch, "E50.0", {"start": v(-6, -6) * mm, "end": v(-6, -20) * mm});
            skLineSegment(sketch, "E50.1", {"start": v(-8, -6) * mm, "end": v(-8, -20) * mm});
            skArc(sketch, "E50.2", {"start": v(-8, -6) * mm, "mid": v(-7, -5) * mm, "end": v(-6, -6) * mm});
            skLineSegment(sketch, "E50.3", {"start": v(6, 11.1) * mm, "end": v(6, 20) * mm});
            skLineSegment(sketch, "E50.4", {"start": v(6, 6) * mm, "end": v(6, 20) * mm});
            skLineSegment(sketch, "E50.5", {"start": v(8, 6) * mm, "end": v(8, 20) * mm});
            skLineSegment(sketch, "E51", {"start": v(6, 20) * mm, "end": v(8, 20) * mm});
            skLineSegment(sketch, "E52", {"start": v(-8, -20) * mm, "end": v(-6, -20) * mm});
            skArc(sketch, "E53.0", {"start": v(8, 6) * mm, "mid": v(7, 5) * mm, "end": v(6, 6) * mm});
            skSolve(sketch);
        }
        {
            var Q0;
            Q0=makeQuery(id+"F12.imprint","IMPRINT",FACE,{"disambiguationData":[TD([[makeQuery(id+"F12.imprint","IMPRINT",EDGE,{"derivedFrom":sQuery(id+"F12.wireOp",EDGE,"E50.0")}),-1.0]])]});
            var Q1;
            Q1=makeQuery(id+"F12.imprint","IMPRINT",FACE,{"disambiguationData":[TD([[makeQuery(id+"F12.imprint","IMPRINT",EDGE,{"derivedFrom":sQuery(id+"F12.wireOp",EDGE,"E50.5")}),1.0]])]});
            extrude(context, id + "F13", {"entities" : qUnion([Q0, Q1]), "operationType" : NewBodyOperationType.ADD, "oppositeDirection" : true, "depth" : (3 - 1.9) * mm, "offsetDistance" : 25 * mm});
        }
        {
            var Q0;
            Q0=makeQuery(id+"F3.opExtrude","CAP_EDGE",EDGE,{"disambiguationData":[OSD([sQuery(id+"F2.wireOp",EDGE,"E34.0")])],"isStart":true});
            var Q1;
            Q1=makeQuery(id+"F13.opExtrude","CAP_EDGE",EDGE,{"disambiguationData":[OSD([sQuery(id+"F12.wireOp",EDGE,"E50.2")])],"isStart":false});
            var Q2;
            Q2=makeQuery(id+"F13.opExtrude","CAP_EDGE",EDGE,{"disambiguationData":[OSD([sQuery(id+"F12.wireOp",EDGE,"E50.6")])],"isStart":false});
            chamfer(context, id + "F14", {"entities" : qUnion([Q0, Q1, Q2]), "width" : 0.3 * mm, "tangentPropagation" : true});
        }
        {
            var Q0;
            Q0=makeQuery(id+"F11.boolean.opBoolean","COPY",FACE,{"derivedFrom":makeQuery(id+"F11.opExtrude","CAP_FACE",FACE,{"disambiguationData":[OSD([sQuery(id+"F0.wireOp",EDGE,"E0.bottom"),sQuery(id+"F0.wireOp",EDGE,"E0.top"),sQuery(id+"F0.wireOp",EDGE,"E0.right"),sQuery(id+"F0.wireOp",EDGE,"E1.bottom"),sQuery(id+"F0.wireOp",EDGE,"E1.top"),sQuery(id+"F0.wireOp",EDGE,"E1.right"),sQuery(id+"F0.wireOp",EDGE,"E2"),sQuery(id+"F0.wireOp",EDGE,"E3"),sQuery(id+"F0.wireOp",EDGE,"E9.bottom"),sQuery(id+"F0.wireOp",EDGE,"E9.top"),sQuery(id+"F0.wireOp",EDGE,"E9.right"),sQuery(id+"F0.wireOp",EDGE,"E10"),sQuery(id+"F0.wireOp",EDGE,"E15.MirrorCS"),sQuery(id+"F0.wireOp",EDGE,"E16.MirrorCS"),sQuery(id+"F0.wireOp",EDGE,"E17.MirrorC"),sQuery(id+"F0.wireOp",EDGE,"E22.MirrorCS"),sQuery(id+"F0.wireOp",EDGE,"E29"),sQuery(id+"F0.wireOp",EDGE,"E31")])],"isStart":false})});
            var sketch = newSketch(context, id + "F15", { "sketchPlane" : qUnion([Q0])});
            skCircle(sketch, "E54.0", {"center": v(-33, -14) * mm, "radius": 2.15 * mm, "construction": true});
            skCircle(sketch, "E54.1", {"center": v(-33, 14) * mm, "radius": 2.15 * mm, "construction": true});
            skCircle(sketch, "E54.2", {"center": v(33, 14) * mm, "radius": 2.15 * mm, "construction": true});
            skCircle(sketch, "E54.3", {"center": v(33, -14) * mm, "radius": 2.15 * mm, "construction": true});
            skCircle(sketch, "E55", {"center": v(-33, 14) * mm, "radius": 3.2 * mm});
            skCircle(sketch, "E56", {"center": v(-33, -14) * mm, "radius": 3.2 * mm});
            skCircle(sketch, "E57", {"center": v(33, -14) * mm, "radius": 3.2 * mm});
            skCircle(sketch, "E58", {"center": v(33, 14) * mm, "radius": 3.2 * mm});
            skSolve(sketch);
        }
        {
            var Q0;
            Q0=makeQuery(id+"F15.imprint","IMPRINT",FACE,{"disambiguationData":[TD([[makeQuery(id+"F15.imprint","IMPRINT",EDGE,{"derivedFrom":sQuery(id+"F15.wireOp",EDGE,"E55")}),1.0]])]});
            var Q1;
            Q1=makeQuery(id+"F15.imprint","IMPRINT",FACE,{"disambiguationData":[TD([[makeQuery(id+"F15.imprint","IMPRINT",EDGE,{"derivedFrom":sQuery(id+"F15.wireOp",EDGE,"E56")}),1.0]])]});
            var Q2;
            Q2=makeQuery(id+"F15.imprint","IMPRINT",FACE,{"disambiguationData":[TD([[makeQuery(id+"F15.imprint","IMPRINT",EDGE,{"derivedFrom":sQuery(id+"F15.wireOp",EDGE,"E57")}),1.0]])]});
            var Q3;
            Q3=makeQuery(id+"F15.imprint","IMPRINT",FACE,{"disambiguationData":[TD([[makeQuery(id+"F15.imprint","IMPRINT",EDGE,{"derivedFrom":sQuery(id+"F15.wireOp",EDGE,"E58")}),1.0]])]});
            extrude(context, id + "F16", {"entities" : qUnion([Q0, Q1, Q2, Q3]), "operationType" : NewBodyOperationType.REMOVE, "oppositeDirection" : true, "depth" : 4.9 * mm, "offsetDistance" : 25 * mm});
        }
        {
            var Q0;
            Q0=makeQuery(id+"F16.boolean.opBoolean","COPY",EDGE,{"derivedFrom":makeQuery(id+"F16.opExtrude","CAP_EDGE",EDGE,{"disambiguationData":[OSD([sQuery(id+"F15.wireOp",EDGE,"E55")])],"isStart":false})});
            var Q1;
            Q1=makeQuery(id+"F16.boolean.opBoolean","COPY",EDGE,{"derivedFrom":makeQuery(id+"F16.opExtrude","CAP_EDGE",EDGE,{"disambiguationData":[OSD([sQuery(id+"F15.wireOp",EDGE,"E56")])],"isStart":false})});
            var Q2;
            Q2=makeQuery(id+"F16.boolean.opBoolean","COPY",EDGE,{"derivedFrom":makeQuery(id+"F16.opExtrude","CAP_EDGE",EDGE,{"disambiguationData":[OSD([sQuery(id+"F15.wireOp",EDGE,"E58")])],"isStart":false})});
            var Q3;
            Q3=makeQuery(id+"F16.boolean.opBoolean","COPY",EDGE,{"derivedFrom":makeQuery(id+"F16.opExtrude","CAP_EDGE",EDGE,{"disambiguationData":[OSD([sQuery(id+"F15.wireOp",EDGE,"E57")])],"isStart":false})});
            chamfer(context, id + "F17", {"entities" : qUnion([Q0, Q1, Q2, Q3]), "chamferType" : ChamferType.TWO_OFFSETS, "width1" : 0.55 * mm, "oppositeDirection" : false, "width2" : 4.9 * mm, "tangentPropagation" : true});
        }
    });
